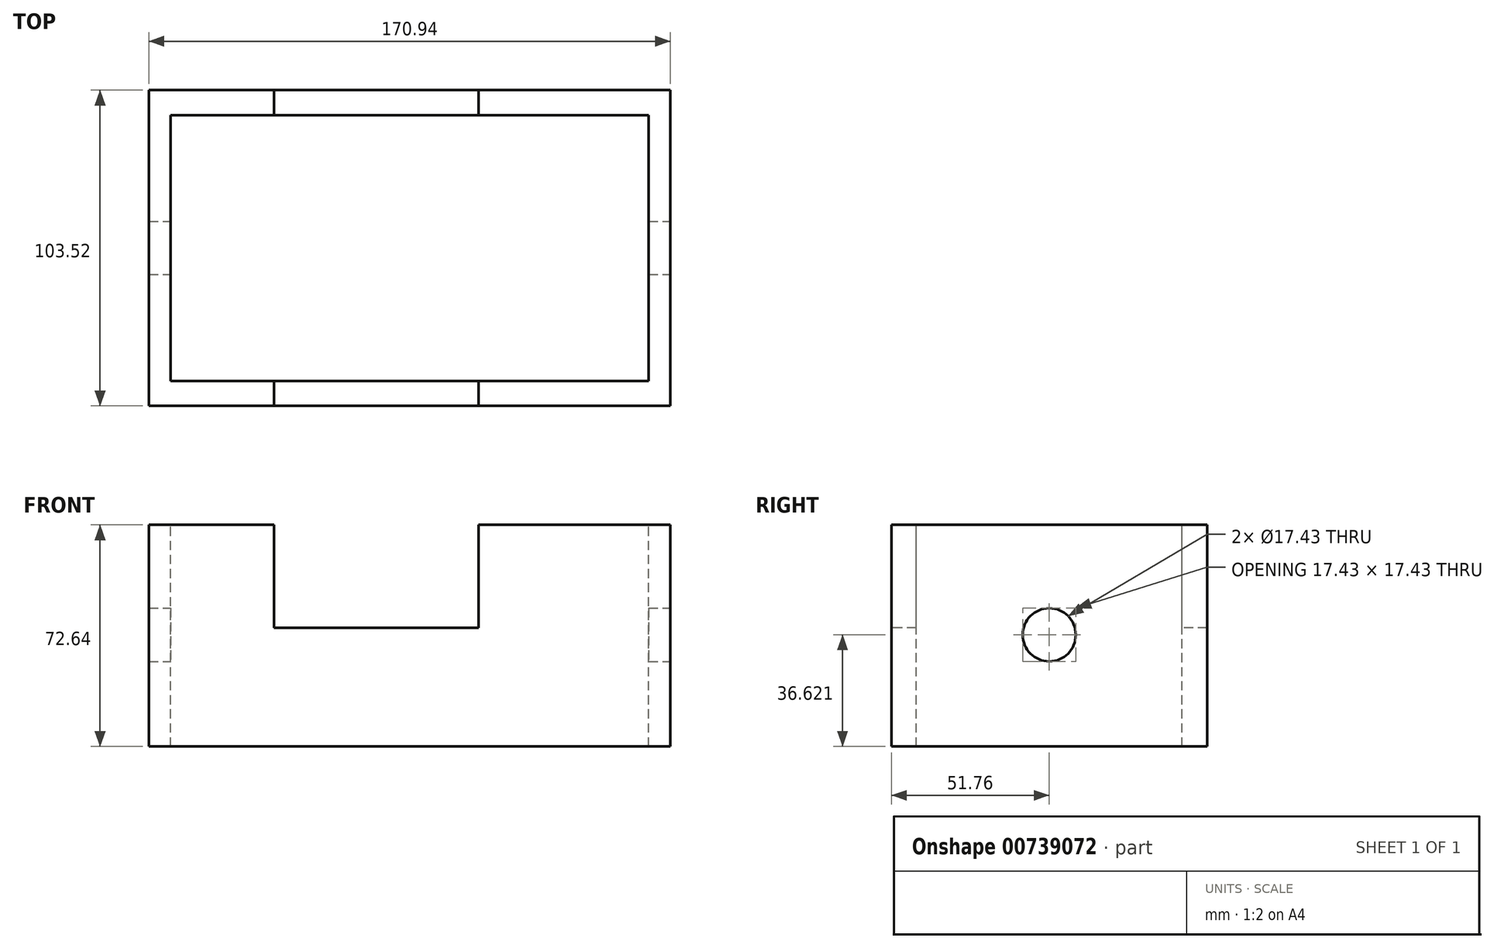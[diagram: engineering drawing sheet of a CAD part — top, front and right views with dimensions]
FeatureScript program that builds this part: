
annotation { "Feature Type Name" : "Feature", "Feature Type Description" : "" }
export const myFeature = defineFeature(function(context is Context, id is Id, definition is map)
    precondition{}
    {
        {
            var Q0;
            Q0=qCreatedBy(makeId("Top.planeOp"),FACE);
            var sketch = newSketch(context, id + "F0", { "sketchPlane" : qUnion([Q0])});
            skLineSegment(sketch, "E0.bottom", {"start": v(85.47, 51.76) * mm, "end": v(-85.47, 51.76) * mm});
            skLineSegment(sketch, "E0.top", {"start": v(85.47, -51.76) * mm, "end": v(-85.47, -51.76) * mm});
            skLineSegment(sketch, "E0.left", {"start": v(85.47, 51.76) * mm, "end": v(85.47, -51.76) * mm});
            skLineSegment(sketch, "E0.right", {"start": v(-85.47, 51.76) * mm, "end": v(-85.47, -51.76) * mm});
            skPoint(sketch, "E0.middle", {"position": v(0, 0) * mm});
            skSolve(sketch);
        }
        {
            var Q0;
            Q0 = qSketchRegion(id + "F0", true);
            extrude(context, id + "F1", {"entities" : qUnion([Q0]), "depth" : 72.64 * mm, "offsetDistance" : 25.4 * mm});
        }
        {
            var Q0;
            Q0=makeQuery(id+"F1.opExtrude","CAP_FACE",FACE,{"disambiguationData":[OSD([sQuery(id+"F0.wireOp",EDGE,"E0.bottom"),sQuery(id+"F0.wireOp",EDGE,"E0.top"),sQuery(id+"F0.wireOp",EDGE,"E0.left"),sQuery(id+"F0.wireOp",EDGE,"E0.right")])],"isStart":false});
            var sketch = newSketch(context, id + "F2", { "sketchPlane" : qUnion([Q0])});
            skLineSegment(sketch, "E1.bottom", {"start": v(78.36, 43.6) * mm, "end": v(-78.36, 43.6) * mm});
            skLineSegment(sketch, "E1.top", {"start": v(78.36, -43.6) * mm, "end": v(-78.36, -43.6) * mm});
            skLineSegment(sketch, "E1.left", {"start": v(78.36, 43.6) * mm, "end": v(78.36, -43.6) * mm});
            skLineSegment(sketch, "E1.right", {"start": v(-78.36, 43.6) * mm, "end": v(-78.36, -43.6) * mm});
            skPoint(sketch, "E1.middle", {"position": v(0, 0) * mm});
            skSolve(sketch);
        }
        {
            var Q0;
            Q0 = qSketchRegion(id + "F2", true);
            extrude(context, id + "F3", {"entities" : qUnion([Q0]), "operationType" : NewBodyOperationType.REMOVE, "oppositeDirection" : true, "depth" : 171.45 * mm, "offsetDistance" : 25.4 * mm});
        }
        {
            var Q0;
            Q0=makeQuery(id+"F1.opExtrude","SWEPT_FACE",FACE,{"disambiguationData":[OSD([sQuery(id+"F0.wireOp",EDGE,"E0.top")])]});
            var sketch = newSketch(context, id + "F4", { "sketchPlane" : qUnion([Q0])});
            skLineSegment(sketch, "E2.bottom", {"start": v(22.56, 72.64) * mm, "end": v(-44.45, 72.64) * mm});
            skLineSegment(sketch, "E2.top", {"start": v(22.56, 38.96) * mm, "end": v(-44.45, 38.96) * mm});
            skLineSegment(sketch, "E2.left", {"start": v(22.56, 72.64) * mm, "end": v(22.56, 38.96) * mm});
            skLineSegment(sketch, "E2.right", {"start": v(-44.45, 72.64) * mm, "end": v(-44.45, 38.96) * mm});
            skPoint(sketch, "E2.middle", {"position": v(-10.95, 55.8) * mm});
            skSolve(sketch);
        }
        {
            var Q0;
            Q0=makeQuery(id+"F4.imprint","IMPRINT",FACE,{"disambiguationData":[TD([[makeQuery(id+"F4.imprint","IMPRINT",EDGE,{"derivedFrom":sQuery(id+"F4.wireOp",EDGE,"E2.bottom")}),1.0]])]});
            var sketch = newSketch(context, id + "F5", { "sketchPlane" : qUnion([Q0])});
            skSolve(sketch);
        }
        {
            var Q0;
            Q0 = qSketchRegion(id + "F5", true);
            var Q1;
            Q1=makeQuery(id+"F4.imprint","IMPRINT",FACE,{"disambiguationData":[TD([[makeQuery(id+"F4.imprint","IMPRINT",EDGE,{"derivedFrom":sQuery(id+"F4.wireOp",EDGE,"E2.bottom")}),1.0]])]});
            extrude(context, id + "F6", {"entities" : qUnion([Q0, Q1]), "operationType" : NewBodyOperationType.REMOVE, "oppositeDirection" : true, "depth" : 172.21 * mm, "offsetDistance" : 25.4 * mm});
        }
        {
            var Q0;
            Q0=makeQuery(id+"F1.opExtrude","SWEPT_FACE",FACE,{"disambiguationData":[OSD([sQuery(id+"F0.wireOp",EDGE,"E0.left")])]});
            var sketch = newSketch(context, id + "F7", { "sketchPlane" : qUnion([Q0])});
            skCircle(sketch, "E3", {"center": v(0, 36.62) * mm, "radius": 8.72 * mm});
            skSolve(sketch);
        }
        {
            var Q0;
            Q0 = qSketchRegion(id + "F7", true);
            extrude(context, id + "F8", {"entities" : qUnion([Q0]), "operationType" : NewBodyOperationType.REMOVE, "oppositeDirection" : true, "depth" : 233.93 * mm, "offsetDistance" : 25.4 * mm});
        }
    });
